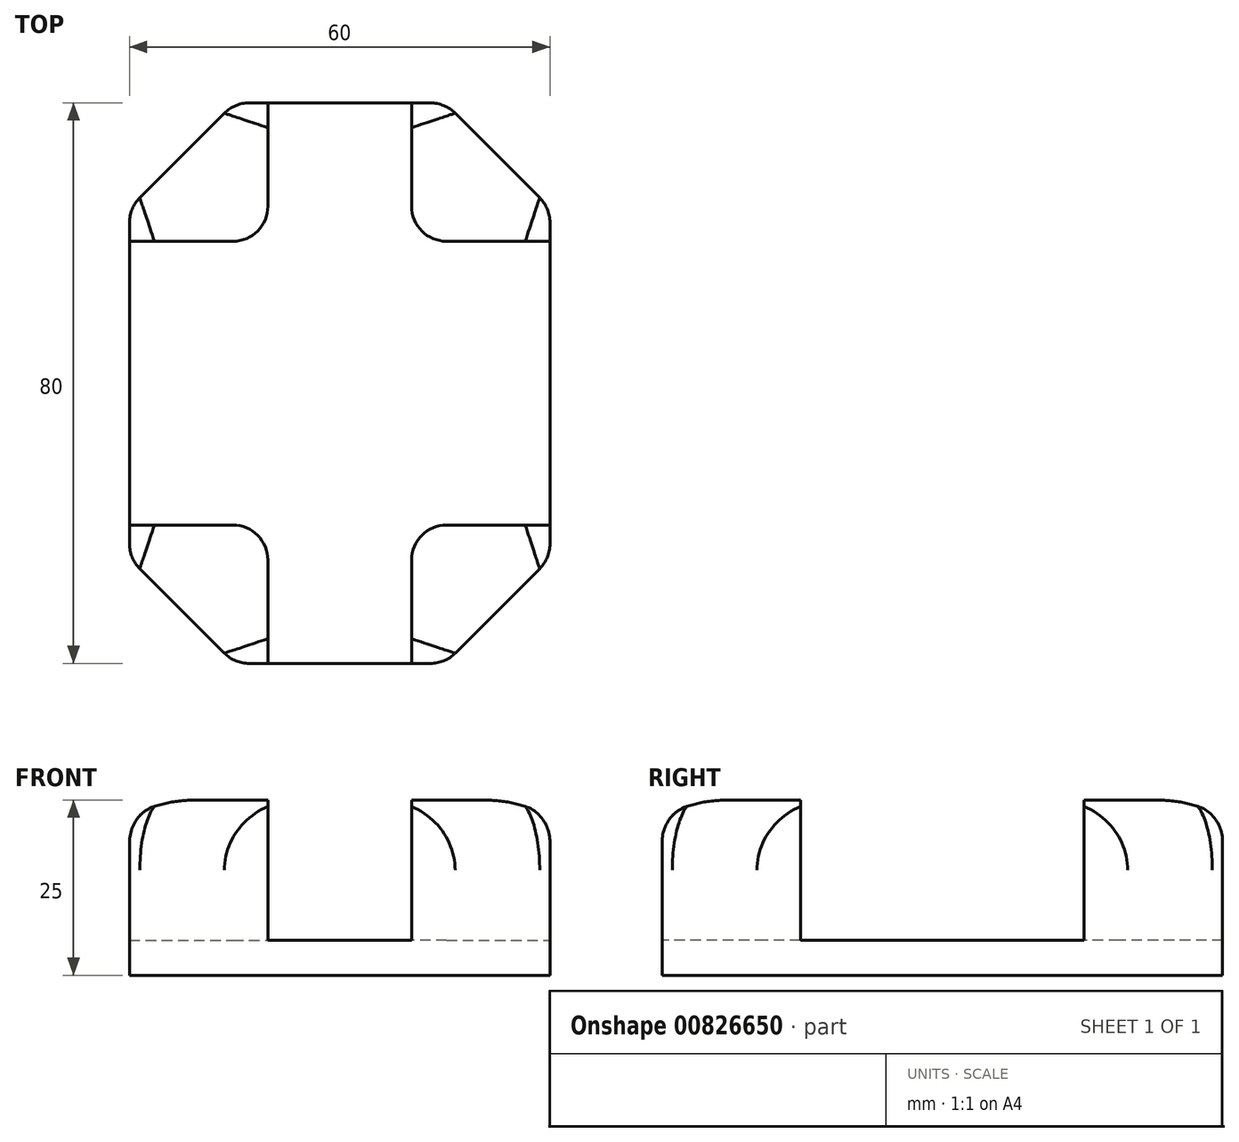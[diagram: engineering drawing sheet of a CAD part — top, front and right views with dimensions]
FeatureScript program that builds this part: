
annotation { "Feature Type Name" : "Feature", "Feature Type Description" : "" }
export const myFeature = defineFeature(function(context is Context, id is Id, definition is map)
    precondition{}
    {
        {
            var Q0;
            Q0=qCreatedBy(makeId("Top.planeOp"),FACE);
            var sketch = newSketch(context, id + "F0", { "sketchPlane" : qUnion([Q0])});
            skLineSegment(sketch, "E0.0", {"start": v(-15, 40) * mm, "end": v(15, 40) * mm});
            skLineSegment(sketch, "E0.1", {"start": v(15, 40) * mm, "end": v(30, 25) * mm});
            skLineSegment(sketch, "E0.2", {"start": v(30, 25) * mm, "end": v(30, -25) * mm});
            skLineSegment(sketch, "E0.3", {"start": v(30, -25) * mm, "end": v(15, -40) * mm});
            skLineSegment(sketch, "E0.4", {"start": v(15, -40) * mm, "end": v(-15, -40) * mm});
            skLineSegment(sketch, "E0.5", {"start": v(-15, -40) * mm, "end": v(-30, -25) * mm});
            skLineSegment(sketch, "E0.6", {"start": v(-30, -25) * mm, "end": v(-30, 25) * mm});
            skLineSegment(sketch, "E0.7", {"start": v(-30, 25) * mm, "end": v(-15, 40) * mm});
            skSolve(sketch);
        }
        {
            var Q0;
            Q0 = qSketchRegion(id + "F0", true);
            extrude(context, id + "F1", {"entities" : qUnion([Q0]), "depth" : 5 * mm, "offsetDistance" : 25 * mm});
        }
        {
            var Q0;
            Q0=makeQuery(id+"F1.opExtrude","CAP_FACE",FACE,{"disambiguationData":[OSD([sQuery(id+"F0.wireOp",EDGE,"E0.0"),sQuery(id+"F0.wireOp",EDGE,"E0.1"),sQuery(id+"F0.wireOp",EDGE,"E0.2"),sQuery(id+"F0.wireOp",EDGE,"E0.3"),sQuery(id+"F0.wireOp",EDGE,"E0.4"),sQuery(id+"F0.wireOp",EDGE,"E0.5"),sQuery(id+"F0.wireOp",EDGE,"E0.6"),sQuery(id+"F0.wireOp",EDGE,"E0.7")])],"isStart":false});
            var sketch = newSketch(context, id + "F2", { "sketchPlane" : qUnion([Q0])});
            skLineSegment(sketch, "E1.bottom", {"start": v(-10.25, 40) * mm, "end": v(10.25, 40) * mm});
            skLineSegment(sketch, "E1.top", {"start": v(-10.25, -40) * mm, "end": v(10.25, -40) * mm});
            skLineSegment(sketch, "E1.left", {"start": v(-10.25, 40) * mm, "end": v(-10.25, -40) * mm});
            skLineSegment(sketch, "E1.right", {"start": v(10.25, 40) * mm, "end": v(10.25, -40) * mm});
            skPoint(sketch, "E1.middle", {"position": v(0, 0) * mm});
            skLineSegment(sketch, "E2.bottom", {"start": v(-30, -20.25) * mm, "end": v(30, -20.25) * mm});
            skLineSegment(sketch, "E2.top", {"start": v(-30, 20.25) * mm, "end": v(30, 20.25) * mm});
            skLineSegment(sketch, "E2.left", {"start": v(-30, -20.25) * mm, "end": v(-30, 20.25) * mm});
            skLineSegment(sketch, "E2.right", {"start": v(30, -20.25) * mm, "end": v(30, 20.25) * mm});
            skSolve(sketch);
        }
        {
            var Q0;
            {var subQ0=makeQuery(id+"F1.opExtrude","CAP_EDGE",EDGE,{"disambiguationData":[OSD([sQuery(id+"F0.wireOp",EDGE,"E0.7")])],"isStart":false});Q0=makeQuery(id+"F2.imprint","IMPRINT",FACE,{"disambiguationData":[TD([[makeQuery(id+"F2.imprint","IMPRINT",EDGE,{"derivedFrom":subQ0}),-1.0]])]});}
            var Q1;
            {var subQ0=makeQuery(id+"F1.opExtrude","CAP_EDGE",EDGE,{"disambiguationData":[OSD([sQuery(id+"F0.wireOp",EDGE,"E0.1")])],"isStart":false});Q1=makeQuery(id+"F2.imprint","IMPRINT",FACE,{"disambiguationData":[TD([[makeQuery(id+"F2.imprint","IMPRINT",EDGE,{"derivedFrom":subQ0}),-1.0]])]});}
            var Q2;
            {var subQ0=makeQuery(id+"F1.opExtrude","CAP_EDGE",EDGE,{"disambiguationData":[OSD([sQuery(id+"F0.wireOp",EDGE,"E0.3")])],"isStart":false});Q2=makeQuery(id+"F2.imprint","IMPRINT",FACE,{"disambiguationData":[TD([[makeQuery(id+"F2.imprint","IMPRINT",EDGE,{"derivedFrom":subQ0}),-1.0]])]});}
            var Q3;
            {var subQ0=makeQuery(id+"F1.opExtrude","CAP_EDGE",EDGE,{"disambiguationData":[OSD([sQuery(id+"F0.wireOp",EDGE,"E0.5")])],"isStart":false});Q3=makeQuery(id+"F2.imprint","IMPRINT",FACE,{"disambiguationData":[TD([[makeQuery(id+"F2.imprint","IMPRINT",EDGE,{"derivedFrom":subQ0}),-1.0]])]});}
            extrude(context, id + "F3", {"entities" : qUnion([Q0, Q1, Q2, Q3]), "operationType" : NewBodyOperationType.ADD, "depth" : 20 * mm, "offsetDistance" : 25 * mm});
        }
        {
            var Q0;
            Q0=makeQuery(id+"F3.opExtrude","CAP_EDGE",EDGE,{"disambiguationData":[OSD([sQuery(id+"F0.wireOp",EDGE,"E0.5")])],"isStart":false});
            var Q1;
            Q1=makeQuery(id+"F3.opExtrude","CAP_EDGE",EDGE,{"disambiguationData":[OSD([sQuery(id+"F0.wireOp",EDGE,"E0.3")])],"isStart":false});
            var Q2;
            Q2=makeQuery(id+"F3.opExtrude","CAP_EDGE",EDGE,{"disambiguationData":[OSD([sQuery(id+"F0.wireOp",EDGE,"E0.1")])],"isStart":false});
            var Q3;
            Q3=makeQuery(id+"F3.opExtrude","CAP_EDGE",EDGE,{"disambiguationData":[OSD([sQuery(id+"F0.wireOp",EDGE,"E0.7")])],"isStart":false});
            fillet(context, id + "F4", {"entities" : qUnion([Q0, Q1, Q2, Q3]), "radius" : 10 * mm, "tangentPropagation" : true, "allowEdgeOverflow" : false});
        }
        {
            var Q0;
            Q0=makeQuery(id+"F3.opExtrude","SWEPT_EDGE",EDGE,{"disambiguationData":[OSD([sQuery(id+"F2.wireOp",EDGE,"E1.left"),sQuery(id+"F2.wireOp",EDGE,"E2.top")])]});
            var Q1;
            Q1=makeQuery(id+"F3.opExtrude","SWEPT_EDGE",EDGE,{"disambiguationData":[OSD([sQuery(id+"F2.wireOp",EDGE,"E1.right"),sQuery(id+"F2.wireOp",EDGE,"E2.top")])]});
            var Q2;
            Q2=makeQuery(id+"F3.opExtrude","SWEPT_EDGE",EDGE,{"disambiguationData":[OSD([sQuery(id+"F2.wireOp",EDGE,"E1.left"),sQuery(id+"F2.wireOp",EDGE,"E2.bottom")])]});
            var Q3;
            Q3=makeQuery(id+"F3.opExtrude","SWEPT_EDGE",EDGE,{"disambiguationData":[OSD([sQuery(id+"F2.wireOp",EDGE,"E1.right"),sQuery(id+"F2.wireOp",EDGE,"E2.bottom")])]});
            fillet(context, id + "F5", {"entities" : qUnion([Q0, Q1, Q2, Q3]), "radius" : 5 * mm, "tangentPropagation" : true, "allowEdgeOverflow" : false});
        }
        {
            var Q0;
            {var subQ0=sQuery(id+"F0.wireOp",EDGE,"E0.7");var subQ1=sQuery(id+"F0.wireOp",EDGE,"E0.6");Q0=makeQuery(id+"F3.boolean.opBoolean","MERGE",EDGE,{"derivedFrom":[makeQuery(id+"F1.opExtrude","SWEPT_EDGE",EDGE,{"disambiguationData":[OSD([subQ1,subQ0])]}),makeQuery(id+"F3.opExtrude","SWEPT_EDGE",EDGE,{"disambiguationData":[OSD([subQ1,subQ0])]})]});}
            var Q1;
            {var subQ0=sQuery(id+"F0.wireOp",EDGE,"E0.7");var subQ1=sQuery(id+"F0.wireOp",EDGE,"E0.0");Q1=makeQuery(id+"F3.boolean.opBoolean","MERGE",EDGE,{"derivedFrom":[makeQuery(id+"F1.opExtrude","SWEPT_EDGE",EDGE,{"disambiguationData":[OSD([subQ1,subQ0])]}),makeQuery(id+"F3.opExtrude","SWEPT_EDGE",EDGE,{"disambiguationData":[OSD([subQ1,subQ0])]})]});}
            var Q2;
            {var subQ0=sQuery(id+"F0.wireOp",EDGE,"E0.1");var subQ1=sQuery(id+"F0.wireOp",EDGE,"E0.0");Q2=makeQuery(id+"F3.boolean.opBoolean","MERGE",EDGE,{"derivedFrom":[makeQuery(id+"F1.opExtrude","SWEPT_EDGE",EDGE,{"disambiguationData":[OSD([subQ1,subQ0])]}),makeQuery(id+"F3.opExtrude","SWEPT_EDGE",EDGE,{"disambiguationData":[OSD([subQ1,subQ0])]})]});}
            var Q3;
            {var subQ0=sQuery(id+"F0.wireOp",EDGE,"E0.2");var subQ1=sQuery(id+"F0.wireOp",EDGE,"E0.1");Q3=makeQuery(id+"F3.boolean.opBoolean","MERGE",EDGE,{"derivedFrom":[makeQuery(id+"F1.opExtrude","SWEPT_EDGE",EDGE,{"disambiguationData":[OSD([subQ1,subQ0])]}),makeQuery(id+"F3.opExtrude","SWEPT_EDGE",EDGE,{"disambiguationData":[OSD([subQ1,subQ0])]})]});}
            var Q4;
            {var subQ0=sQuery(id+"F0.wireOp",EDGE,"E0.3");var subQ1=sQuery(id+"F0.wireOp",EDGE,"E0.2");Q4=makeQuery(id+"F3.boolean.opBoolean","MERGE",EDGE,{"derivedFrom":[makeQuery(id+"F1.opExtrude","SWEPT_EDGE",EDGE,{"disambiguationData":[OSD([subQ1,subQ0])]}),makeQuery(id+"F3.opExtrude","SWEPT_EDGE",EDGE,{"disambiguationData":[OSD([subQ1,subQ0])]})]});}
            var Q5;
            {var subQ0=sQuery(id+"F0.wireOp",EDGE,"E0.4");var subQ1=sQuery(id+"F0.wireOp",EDGE,"E0.3");Q5=makeQuery(id+"F3.boolean.opBoolean","MERGE",EDGE,{"derivedFrom":[makeQuery(id+"F1.opExtrude","SWEPT_EDGE",EDGE,{"disambiguationData":[OSD([subQ1,subQ0])]}),makeQuery(id+"F3.opExtrude","SWEPT_EDGE",EDGE,{"disambiguationData":[OSD([subQ1,subQ0])]})]});}
            var Q6;
            {var subQ0=sQuery(id+"F0.wireOp",EDGE,"E0.5");var subQ1=sQuery(id+"F0.wireOp",EDGE,"E0.4");Q6=makeQuery(id+"F3.boolean.opBoolean","MERGE",EDGE,{"derivedFrom":[makeQuery(id+"F1.opExtrude","SWEPT_EDGE",EDGE,{"disambiguationData":[OSD([subQ1,subQ0])]}),makeQuery(id+"F3.opExtrude","SWEPT_EDGE",EDGE,{"disambiguationData":[OSD([subQ1,subQ0])]})]});}
            var Q7;
            {var subQ0=sQuery(id+"F0.wireOp",EDGE,"E0.6");var subQ1=sQuery(id+"F0.wireOp",EDGE,"E0.5");Q7=makeQuery(id+"F3.boolean.opBoolean","MERGE",EDGE,{"derivedFrom":[makeQuery(id+"F1.opExtrude","SWEPT_EDGE",EDGE,{"disambiguationData":[OSD([subQ1,subQ0])]}),makeQuery(id+"F3.opExtrude","SWEPT_EDGE",EDGE,{"disambiguationData":[OSD([subQ1,subQ0])]})]});}
            fillet(context, id + "F6", {"entities" : qUnion([Q0, Q1, Q2, Q3, Q4, Q5, Q6, Q7]), "radius" : 5 * mm, "tangentPropagation" : true, "allowEdgeOverflow" : false});
        }
    });
